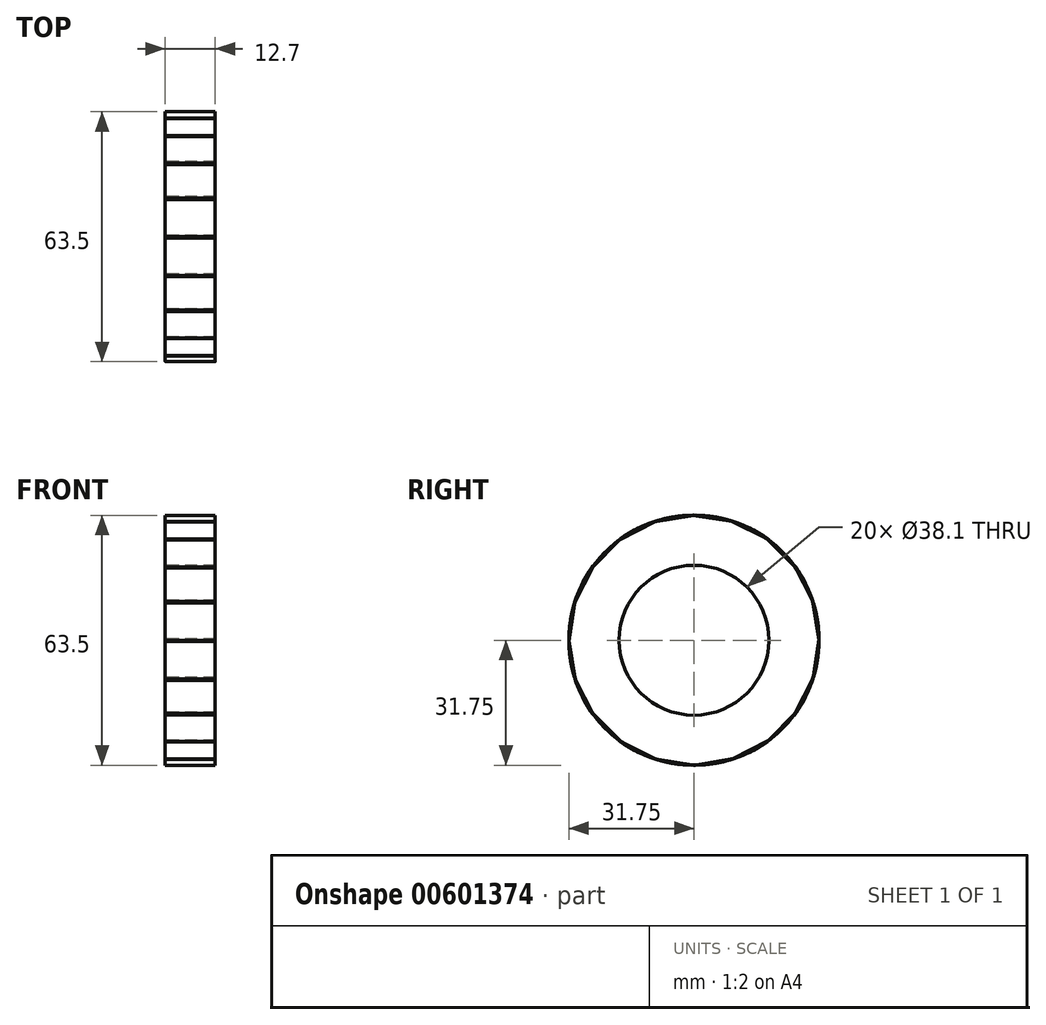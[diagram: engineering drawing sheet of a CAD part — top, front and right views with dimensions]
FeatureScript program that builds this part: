
annotation { "Feature Type Name" : "Feature", "Feature Type Description" : "" }
export const myFeature = defineFeature(function(context is Context, id is Id, definition is map)
    precondition{}
    {
        {
            var Q0;
            Q0=qCreatedBy(makeId("Right.planeOp"),FACE);
            var sketch = newSketch(context, id + "F0", { "sketchPlane" : qUnion([Q0])});
            skCircle(sketch, "E0", {"center": v(0, 0) * mm, "radius": 19.05 * mm});
            skCircle(sketch, "E1", {"center": v(0, 0) * mm, "radius": 31.75 * mm});
            skLineSegment(sketch, "E2", {"start": v(0, 31.75) * mm, "end": v(-10.16, 30.08) * mm});
            skArc(sketch, "E3", {"start": v(-10.16, 30.08) * mm, "mid": v(-8.72, 37.23) * mm, "end": v(-2.9, 41.63) * mm});
            skArc(sketch, "E4", {"start": v(0, 31.75) * mm, "mid": v(-4.8, 38.87) * mm, "end": v(-13.34, 39.87) * mm});
            skSolve(sketch);
        }
        {
            var Q0;
            {var subQ0=sQuery(id+"F0.wireOp",EDGE,"E4");var subQ4=sQuery(id+"F0.wireOp",EDGE,"E3");var subQ6=makeQuery(id+"F0.imprint","INTERSECT",VERTEX,{"derivedFrom":[subQ4,subQ0]});Q0=makeQuery(id+"F0.imprint","IMPRINT",FACE,{"disambiguationData":[TD([[makeQuery(id+"F0.imprint","IMPRINT",EDGE,{"disambiguationData":[TD([[subQ6,1.0]])],"derivedFrom":subQ4}),-1.0]])]});}
            var Q1;
            Q1=makeQuery(id+"F0.imprint","IMPRINT",FACE,{"disambiguationData":[TD([[makeQuery(id+"F0.imprint","IMPRINT",EDGE,{"derivedFrom":sQuery(id+"F0.wireOp",EDGE,"E0")}),-1.0]])]});
            extrude(context, id + "F1", {"entities" : qUnion([Q0, Q1]), "depth" : 12.7 * mm, "offsetDistance" : 25.4 * mm});
        }
        {
            var Q0;
            Q0=makeQuery(id+"F1.opExtrude","SWEPT_BODY",BODY,{"disambiguationData":[OSD([sQuery(id+"F0.wireOp",EDGE,"E1"),sQuery(id+"F0.wireOp",EDGE,"E3"),sQuery(id+"F0.wireOp",EDGE,"E4")])]});
            var Q1;
            Q1=makeQuery(id+"F1.opExtrude","SWEPT_BODY",BODY,{"disambiguationData":[OSD([sQuery(id+"F0.wireOp",EDGE,"E0"),sQuery(id+"F0.wireOp",EDGE,"E1"),sQuery(id+"F0.wireOp",EDGE,"E2")])]});
            var Q2;
            Q2=makeQuery(id+"F1.opExtrude","CAP_EDGE",EDGE,{"disambiguationData":[OSD([sQuery(id+"F0.wireOp",EDGE,"E0")])],"isStart":false});
            circularPattern(context, id + "F2", {"entities" : qUnion([Q0, Q1]), "axis" : qUnion([Q2]), "angle" : 360 * degree, "instanceCount" : 20, "equalSpace" : true});
        }
    });
